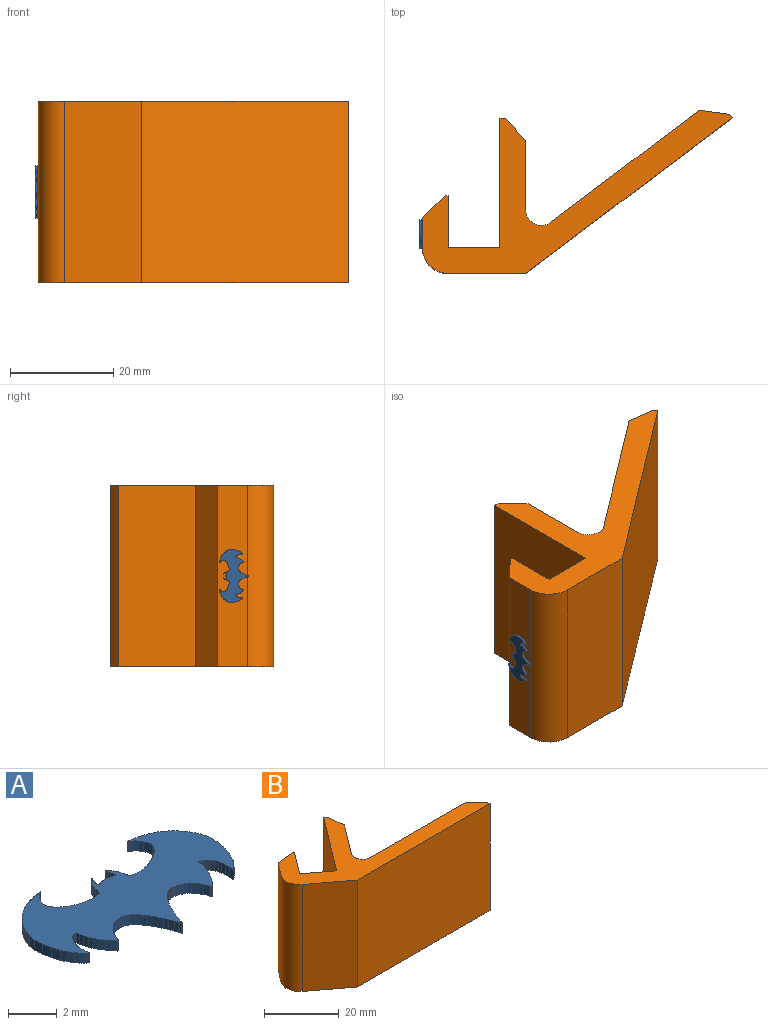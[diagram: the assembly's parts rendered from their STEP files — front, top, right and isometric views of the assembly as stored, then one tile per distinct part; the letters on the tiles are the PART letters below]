
ASSEMBLY  parts=2 mates=1
PART A: 225 faces, bbox 10.2x5.7x0.5 mm
  f0: cylinder r=2.47mm len=0.5mm, axis (0,0,1), area 0mm2, adj f1,f222,f223,f224
  f1: cylinder r=1.36mm len=0.5mm, axis (0,0,1), area 0.1mm2, adj f0,f2,f223,f224
  f2: cylinder r=7.6mm len=0.5mm, axis (0,0,1), area 0.1mm2, adj f1,f3,f223,f224
  f3: cylinder r=7.45mm len=0.5mm, axis (0,0,1), area 0.1mm2, adj f2,f4,f223,f224
  f4: cylinder r=1.87mm len=0.5mm, axis (0,0,1), area 0.1mm2, adj f3,f5,f223,f224
  f5: cylinder r=2.14mm len=0.5mm, axis (0,0,1), area 0.1mm2, adj f4,f6,f223,f224
  f6: cylinder r=2.99mm len=0.5mm, axis (0,0,1), area 0.1mm2, adj f5,f7,f223,f224
  f7: cylinder r=3.14mm len=0.5mm, axis (0,0,1), area 0.2mm2, adj f6,f8,f223,f224
  f8: cylinder r=2.81mm len=0.5mm, axis (0,0,1), area 0.1mm2, adj f7,f9,f223,f224
  f9: cylinder r=1.36mm len=0.5mm, axis (0,0,1), area 0.1mm2, adj f8,f10,f223,f224
  f10: cylinder r=4.82mm len=0.5mm, axis (0,0,1), area 0.1mm2, adj f9,f11,f223,f224
  f11: cylinder r=4.88mm len=0.5mm, axis (0,0,1), area 0.1mm2, adj f10,f12,f223,f224
  f12: cylinder r=1.99mm len=0.5mm, axis (0,0,1), area 0.1mm2, adj f11,f13,f223,f224
  f13: cylinder r=1.85mm len=0.5mm, axis (0,0,1), area 0.1mm2, adj f12,f14,f223,f224
  f14: cylinder r=3.8mm len=0.5mm, axis (0,0,1), area 0.1mm2, adj f13,f15,f223,f224
  f15: cylinder r=3.71mm len=0.5mm, axis (0,0,1), area 0.1mm2, adj f14,f16,f223,f224
  f16: cylinder r=1.26mm len=0.5mm, axis (0,0,1), area 0.1mm2, adj f15,f17,f223,f224
  f17: cylinder r=1.37mm len=0.5mm, axis (0,0,1), area 0.2mm2, adj f16,f18,f223,f224
  f18: cylinder r=3.17mm len=0.5mm, axis (0,0,1), area 0.2mm2, adj f17,f19,f223,f224
  f19: cylinder r=3.6mm len=0.5mm, axis (0,0,1), area 0.2mm2, adj f18,f20,f223,f224
  f20: cylinder r=3.26mm len=0.5mm, axis (0,0,1), area 0.2mm2, adj f19,f21,f223,f224
  f21: cylinder r=2.06mm len=0.5mm, axis (0,0,1), area 0.1mm2, adj f20,f22,f223,f224
  f22: cylinder r=3.13mm len=0.5mm, axis (0,0,1), area 0.1mm2, adj f21,f23,f223,f224
  f23: cylinder r=2.96mm len=0.5mm, axis (0,0,1), area 0.1mm2, adj f22,f24,f223,f224
  f24: cylinder r=1.3mm len=0.5mm, axis (0,0,1), area 0.1mm2, adj f23,f25,f223,f224
  f25: plane 0.5x0.09mm, normal (-0.63,-0.77,0), area 0.1mm2, adj f24,f26,f223,f224
  f26: plane 0.5x0.26mm, normal (1,0.05,0), area 0.1mm2, adj f25,f27,f223,f224
  f27: cylinder r=2.86mm len=0.5mm, axis (0,0,1), area 0.1mm2, adj f26,f28,f223,f224
  f28: cylinder r=1.47mm len=0.5mm, axis (0,0,1), area 0.1mm2, adj f27,f29,f223,f224
  f29: cylinder r=1.17mm len=0.5mm, axis (0,0,1), area 0.1mm2, adj f28,f30,f223,f224
  f30: cylinder r=1.1mm len=0.5mm, axis (0,0,1), area 0.1mm2, adj f29,f31,f223,f224
  f31: cylinder r=1.32mm len=0.5mm, axis (0,0,1), area 0.1mm2, adj f30,f32,f223,f224
  f32: cylinder r=0.63mm len=0.5mm, axis (0,0,1), area 0.1mm2, adj f31,f33,f223,f224
  f33: cylinder r=0.5mm len=0.5mm, axis (0,0,1), area 0.1mm2, adj f32,f34,f223,f224
  f34: cylinder r=0.57mm len=0.5mm, axis (0,0,1), area 0.1mm2, adj f33,f35,f223,f224
  f35: plane 0.5x0.07mm, normal (0.18,-0.98,0), area 0mm2, adj f34,f36,f223,f224
  f36: plane 0.5x0.19mm, normal (-0.99,-0.13,0), area 0.1mm2, adj f35,f37,f223,f224
  f37: cylinder r=1.78mm len=0.5mm, axis (0,0,1), area 0.1mm2, adj f36,f38,f223,f224
  f38: cylinder r=1.73mm len=0.5mm, axis (0,0,1), area 0.1mm2, adj f37,f39,f223,f224
  f39: cylinder r=2.05mm len=0.5mm, axis (0,0,1), area 0.1mm2, adj f38,f40,f223,f224
  f40: cylinder r=3.63mm len=0.5mm, axis (0,0,1), area 0.1mm2, adj f39,f41,f223,f224
  f41: cylinder r=3.24mm len=0.5mm, axis (0,0,1), area 0.1mm2, adj f40,f42,f223,f224
  f42: cylinder r=6.22mm len=0.5mm, axis (0,0,1), area 0.1mm2, adj f41,f43,f223,f224
  f43: cylinder r=16.14mm len=0.5mm, axis (0,0,1), area 0.1mm2, adj f42,f44,f223,f224
  f44: cylinder r=0.06mm len=0.5mm, axis (0,0,1), area 0mm2, adj f43,f45,f223,f224
  f45: cylinder r=0.01mm len=0.5mm, axis (0,0,1), area 0mm2, adj f44,f46,f223,f224
  f46: cylinder r=0.57mm len=0.5mm, axis (0,0,1), area 0mm2, adj f45,f47,f223,f224
  f47: cylinder r=0.56mm len=0.5mm, axis (0,0,1), area 0mm2, adj f46,f48,f223,f224
  f48: cylinder r=1.02mm len=0.5mm, axis (0,0,1), area 0mm2, adj f47,f49,f223,f224
  f49: cylinder r=1.42mm len=0.5mm, axis (0,0,1), area 0.1mm2, adj f48,f50,f223,f224
  f50: cylinder r=1.9mm len=0.5mm, axis (0,0,1), area 0.1mm2, adj f49,f51,f223,f224
  f51: cylinder r=1.82mm len=0.5mm, axis (0,0,1), area 0.1mm2, adj f50,f52,f223,f224
  f52: cylinder r=1.13mm len=0.5mm, axis (0,0,1), area 0.1mm2, adj f51,f53,f223,f224
  f53: cylinder r=1.01mm len=0.5mm, axis (0,0,1), area 0.1mm2, adj f52,f54,f223,f224
  f54: cylinder r=1.15mm len=0.5mm, axis (0,0,1), area 0.1mm2, adj f53,f55,f223,f224
  f55: cylinder r=1.04mm len=0.5mm, axis (0,0,1), area 0.1mm2, adj f54,f56,f223,f224
  f56: cylinder r=0.56mm len=0.5mm, axis (0,0,1), area 0.1mm2, adj f55,f57,f223,f224
  f57: cylinder r=0.72mm len=0.5mm, axis (0,0,1), area 0.1mm2, adj f56,f58,f223,f224
  f58: cylinder r=1.73mm len=0.5mm, axis (0,0,1), area 0.2mm2, adj f57,f59,f223,f224
  f59: cylinder r=2.47mm len=0.5mm, axis (0,0,1), area 0.2mm2, adj f58,f60,f223,f224
  f60: cylinder r=4.3mm len=0.5mm, axis (0,0,1), area 0.2mm2, adj f59,f61,f223,f224
  f61: cylinder r=5.97mm len=0.5mm, axis (0,0,1), area 0.1mm2, adj f60,f62,f223,f224
  f62: cylinder r=7.82mm len=0.5mm, axis (0,0,1), area 0.1mm2, adj f61,f63,f223,f224
  f63: cylinder r=7.49mm len=0.5mm, axis (0,0,1), area 0.1mm2, adj f62,f64,f223,f224
  f64: cylinder r=4.46mm len=0.5mm, axis (0,0,1), area 0.1mm2, adj f63,f65,f223,f224
  f65: cylinder r=2.06mm len=0.5mm, axis (0,0,1), area 0mm2, adj f64,f66,f223,f224
  f66: cylinder r=1.1mm len=0.5mm, axis (0,0,1), area 0mm2, adj f65,f67,f223,f224
  f67: cylinder r=1.96mm len=0.5mm, axis (0,0,1), area 0mm2, adj f66,f68,f223,f224
  f68: cylinder r=0.01mm len=0.5mm, axis (0,0,1), area 0mm2, adj f67,f69,f223,f224
  f69: cylinder r=1.96mm len=0.5mm, axis (0,0,1), area 0mm2, adj f68,f70,f223,f224
  f70: cylinder r=1.1mm len=0.5mm, axis (0,0,1), area 0mm2, adj f69,f71,f223,f224
  f71: cylinder r=2.06mm len=0.5mm, axis (0,0,1), area 0mm2, adj f70,f72,f223,f224
  f72: cylinder r=5.3mm len=0.5mm, axis (0,0,1), area 0.2mm2, adj f71,f73,f223,f224
  f73: cylinder r=6.68mm len=0.5mm, axis (0,0,1), area 0.2mm2, adj f72,f74,f223,f224
  f74: cylinder r=6.25mm len=0.5mm, axis (0,0,1), area 0.2mm2, adj f73,f75,f223,f224
  f75: cylinder r=3.36mm len=0.5mm, axis (0,0,1), area 0.2mm2, adj f74,f76,f223,f224
  f76: cylinder r=2.6mm len=0.5mm, axis (0,0,1), area 0.1mm2, adj f75,f77,f223,f224
  f77: cylinder r=1.69mm len=0.5mm, axis (0,0,1), area 0.1mm2, adj f76,f78,f223,f224
  f78: cylinder r=1.29mm len=0.5mm, axis (0,0,1), area 0.1mm2, adj f77,f79,f223,f224
  f79: cylinder r=0.66mm len=0.5mm, axis (0,0,1), area 0.1mm2, adj f78,f80,f223,f224
  f80: cylinder r=0.52mm len=0.5mm, axis (0,0,1), area 0.1mm2, adj f79,f81,f223,f224
  f81: cylinder r=1.14mm len=0.5mm, axis (0,0,1), area 0.1mm2, adj f80,f82,f223,f224
  f82: cylinder r=1.25mm len=0.5mm, axis (0,0,1), area 0.1mm2, adj f81,f83,f223,f224
  f83: cylinder r=0.97mm len=0.5mm, axis (0,0,1), area 0.1mm2, adj f82,f84,f223,f224
  f84: cylinder r=1.13mm len=0.5mm, axis (0,0,1), area 0.1mm2, adj f83,f85,f223,f224
  f85: cylinder r=1.82mm len=0.5mm, axis (0,0,1), area 0.1mm2, adj f84,f86,f223,f224
  f86: cylinder r=1.9mm len=0.5mm, axis (0,0,1), area 0.1mm2, adj f85,f87,f223,f224
  f87: cylinder r=1.42mm len=0.5mm, axis (0,0,1), area 0.1mm2, adj f86,f88,f223,f224
  f88: cylinder r=1.02mm len=0.5mm, axis (0,0,1), area 0mm2, adj f87,f89,f223,f224
  f89: cylinder r=0.56mm len=0.5mm, axis (0,0,1), area 0mm2, adj f88,f90,f223,f224
  f90: cylinder r=0.57mm len=0.5mm, axis (0,0,1), area 0mm2, adj f89,f91,f223,f224
  f91: cylinder r=0.01mm len=0.5mm, axis (0,0,1), area 0mm2, adj f90,f92,f223,f224
  f92: cylinder r=0.03mm len=0.5mm, axis (0,0,1), area 0mm2, adj f91,f93,f223,f224
  f93: cylinder r=6mm len=0.5mm, axis (0,0,1), area 0.1mm2, adj f92,f94,f223,f224
  f94: cylinder r=3.62mm len=0.5mm, axis (0,0,1), area 0.1mm2, adj f93,f95,f223,f224
  f95: cylinder r=6.4mm len=0.5mm, axis (0,0,1), area 0.1mm2, adj f94,f96,f223,f224
  f96: cylinder r=3.88mm len=0.5mm, axis (0,0,1), area 0.2mm2, adj f95,f97,f223,f224
  f97: cylinder r=2.69mm len=0.5mm, axis (0,0,1), area 0.2mm2, adj f96,f98,f223,f224
  f98: cylinder r=2.18mm len=0.5mm, axis (0,0,1), area 0.1mm2, adj f97,f99,f223,f224
  f99: cylinder r=1.38mm len=0.5mm, axis (0,0,1), area 0.1mm2, adj f98,f100,f223,f224
  f100: plane 0.5x0.15mm, normal (1,-0.09,0), area 0.1mm2, adj f99,f101,f223,f224
  f101: plane 0.5x0.07mm, normal (-0.18,-0.98,0), area 0mm2, adj f100,f102,f223,f224
  f102: cylinder r=0.57mm len=0.5mm, axis (0,0,1), area 0.1mm2, adj f101,f103,f223,f224
  f103: cylinder r=0.5mm len=0.5mm, axis (0,0,1), area 0.1mm2, adj f102,f104,f223,f224
  f104: cylinder r=0.62mm len=0.5mm, axis (0,0,1), area 0.1mm2, adj f103,f105,f223,f224
  f105: cylinder r=1.32mm len=0.5mm, axis (0,0,1), area 0.1mm2, adj f104,f106,f223,f224
  f106: cylinder r=1.1mm len=0.5mm, axis (0,0,1), area 0.1mm2, adj f105,f107,f223,f224
  f107: cylinder r=1.17mm len=0.5mm, axis (0,0,1), area 0.1mm2, adj f106,f108,f223,f224
  f108: cylinder r=1.47mm len=0.5mm, axis (0,0,1), area 0.1mm2, adj f107,f109,f223,f224
  f109: cylinder r=2.84mm len=0.5mm, axis (0,0,1), area 0.1mm2, adj f108,f110,f223,f224
  f110: plane 0.5x0.26mm, normal (-1,0.05,0), area 0.1mm2, adj f109,f111,f223,f224
  f111: plane 0.5x0.08mm, normal (0.62,-0.78,0), area 0.1mm2, adj f110,f112,f223,f224
  f112: cylinder r=0.87mm len=0.5mm, axis (0,0,1), area 0.1mm2, adj f111,f113,f223,f224
  f113: cylinder r=2.65mm len=0.5mm, axis (0,0,1), area 0.1mm2, adj f112,f114,f223,f224
  f114: cylinder r=3.1mm len=0.5mm, axis (0,0,1), area 0.1mm2, adj f113,f115,f223,f224
  f115: cylinder r=3.08mm len=0.5mm, axis (0,0,1), area 0.1mm2, adj f114,f116,f223,f224
  f116: cylinder r=2.19mm len=0.5mm, axis (0,0,1), area 0.2mm2, adj f115,f117,f223,f224
  f117: cylinder r=3.23mm len=0.5mm, axis (0,0,1), area 0.2mm2, adj f116,f118,f223,f224
  f118: cylinder r=3.43mm len=0.5mm, axis (0,0,1), area 0.2mm2, adj f117,f119,f223,f224
  f119: cylinder r=3.06mm len=0.5mm, axis (0,0,1), area 0.2mm2, adj f118,f120,f223,f224
  f120: cylinder r=2.13mm len=0.5mm, axis (0,0,1), area 0.1mm2, adj f119,f121,f223,f224
  f121: cylinder r=1.28mm len=0.5mm, axis (0,0,1), area 0.1mm2, adj f120,f122,f223,f224
  f122: cylinder r=1.35mm len=0.5mm, axis (0,0,1), area 0.1mm2, adj f121,f123,f223,f224
  f123: cylinder r=2.58mm len=0.5mm, axis (0,0,1), area 0.1mm2, adj f122,f124,f223,f224
  f124: cylinder r=4.55mm len=0.5mm, axis (0,0,1), area 0.1mm2, adj f123,f125,f223,f224
  f125: cylinder r=1.94mm len=0.5mm, axis (0,0,1), area 0.1mm2, adj f124,f126,f223,f224
  f126: cylinder r=2mm len=0.5mm, axis (0,0,1), area 0.1mm2, adj f125,f127,f223,f224
  f127: cylinder r=5.08mm len=0.5mm, axis (0,0,1), area 0.1mm2, adj f126,f128,f223,f224
  f128: cylinder r=2.72mm len=0.5mm, axis (0,0,1), area 0.2mm2, adj f127,f129,f223,f224
  f129: cylinder r=2.51mm len=0.5mm, axis (0,0,1), area 0.2mm2, adj f128,f130,f223,f224
  f130: cylinder r=2.57mm len=0.5mm, axis (0,0,1), area 0.2mm2, adj f129,f131,f223,f224
  f131: cylinder r=2.99mm len=0.5mm, axis (0,0,1), area 0.2mm2, adj f130,f132,f223,f224
  f132: cylinder r=3.6mm len=0.5mm, axis (0,0,1), area 0.1mm2, adj f131,f133,f223,f224
  f133: cylinder r=4.3mm len=0.5mm, axis (0,0,1), area 0.1mm2, adj f132,f134,f223,f224
  f134: cylinder r=12.42mm len=0.5mm, axis (0,0,1), area 0.1mm2, adj f133,f135,f223,f224
  f135: cylinder r=0.01mm len=0.5mm, axis (0,0,1), area 0mm2, adj f134,f136,f223,f224
  f136: cylinder r=0.01mm len=0.5mm, axis (0,0,1), area 0mm2, adj f135,f137,f223,f224
  f137: cylinder r=1.56mm len=0.5mm, axis (0,0,1), area 0mm2, adj f136,f138,f223,f224
  f138: cylinder r=0.91mm len=0.5mm, axis (0,0,1), area 0mm2, adj f137,f139,f223,f224
  f139: cylinder r=1.65mm len=0.5mm, axis (0,0,1), area 0mm2, adj f138,f140,f223,f224
  f140: cylinder r=0.8mm len=0.5mm, axis (0,0,1), area 0.1mm2, adj f139,f141,f223,f224
  f141: cylinder r=1mm len=0.5mm, axis (0,0,1), area 0.1mm2, adj f140,f142,f223,f224
  f142: cylinder r=0.89mm len=0.5mm, axis (0,0,1), area 0.1mm2, adj f141,f143,f223,f224
  f143: cylinder r=0.45mm len=0.5mm, axis (0,0,1), area 0.1mm2, adj f142,f144,f223,f224
  f144: cylinder r=0.44mm len=0.5mm, axis (0,0,1), area 0.1mm2, adj f143,f145,f223,f224
  f145: cylinder r=1.11mm len=0.5mm, axis (0,0,1), area 0.1mm2, adj f144,f146,f223,f224
  f146: cylinder r=1.34mm len=0.5mm, axis (0,0,1), area 0.1mm2, adj f145,f147,f223,f224
  f147: cylinder r=1.46mm len=0.5mm, axis (0,0,1), area 0.1mm2, adj f146,f148,f223,f224
  f148: cylinder r=1.73mm len=0.5mm, axis (0,0,1), area 0.1mm2, adj f147,f149,f223,f224
  f149: cylinder r=4.09mm len=0.5mm, axis (0,0,1), area 0.1mm2, adj f148,f150,f223,f224
  f150: cylinder r=4.03mm len=0.5mm, axis (0,0,1), area 0.1mm2, adj f149,f151,f223,f224
  f151: cylinder r=1.36mm len=0.5mm, axis (0,0,1), area 0.1mm2, adj f150,f152,f223,f224
  f152: cylinder r=2.03mm len=0.5mm, axis (0,0,1), area 0.2mm2, adj f151,f153,f223,f224
  f153: cylinder r=2.3mm len=0.5mm, axis (0,0,1), area 0.2mm2, adj f152,f154,f223,f224
  f154: cylinder r=2.08mm len=0.5mm, axis (0,0,1), area 0.1mm2, adj f153,f155,f223,f224
  f155: cylinder r=0.17mm len=0.5mm, axis (0,0,1), area 0.1mm2, adj f154,f156,f223,f224
  f156: cylinder r=0.11mm len=0.5mm, axis (0,0,1), area 0mm2, adj f155,f157,f223,f224
  f157: cylinder r=1.9mm len=0.5mm, axis (0,0,1), area 0mm2, adj f156,f158,f223,f224
  f158: cylinder r=1.96mm len=0.5mm, axis (0,0,1), area 0mm2, adj f157,f159,f223,f224
  f159: cylinder r=2.56mm len=0.5mm, axis (0,0,1), area 0mm2, adj f158,f160,f223,f224
  f160: cylinder r=1.85mm len=0.5mm, axis (0,0,1), area 0.1mm2, adj f159,f161,f223,f224
  f161: cylinder r=0.86mm len=0.5mm, axis (0,0,1), area 0.1mm2, adj f160,f162,f223,f224
  f162: cylinder r=0.76mm len=0.5mm, axis (0,0,1), area 0.1mm2, adj f161,f163,f223,f224
  f163: cylinder r=1.16mm len=0.5mm, axis (0,0,1), area 0.1mm2, adj f162,f164,f223,f224
  f164: cylinder r=2.82mm len=0.5mm, axis (0,0,1), area 0.1mm2, adj f163,f165,f223,f224
  f165: cylinder r=0.1mm len=0.5mm, axis (0,0,1), area 0mm2, adj f164,f166,f223,f224
  f166: cylinder r=0.01mm len=0.5mm, axis (0,0,1), area 0mm2, adj f165,f167,f223,f224
  f167: cylinder r=0.35mm len=0.5mm, axis (0,0,1), area 0mm2, adj f166,f168,f223,f224
  f168: cylinder r=0.44mm len=0.5mm, axis (0,0,1), area 0mm2, adj f167,f169,f223,f224
  f169: cylinder r=1.93mm len=0.5mm, axis (0,0,1), area 0.1mm2, adj f168,f170,f223,f224
  f170: cylinder r=1.92mm len=0.5mm, axis (0,0,1), area 0.1mm2, adj f169,f171,f223,f224
  f171: cylinder r=0.48mm len=0.5mm, axis (0,0,1), area 0mm2, adj f170,f172,f223,f224
  f172: cylinder r=0.25mm len=0.5mm, axis (0,0,1), area 0mm2, adj f171,f173,f223,f224
  f173: cylinder r=0.01mm len=0.5mm, axis (0,0,1), area 0mm2, adj f172,f174,f223,f224
  f174: cylinder r=0.09mm len=0.5mm, axis (0,0,1), area 0mm2, adj f173,f175,f223,f224
  f175: cylinder r=17.8mm len=0.5mm, axis (0,0,1), area 0.1mm2, adj f174,f176,f223,f224
  f176: cylinder r=0.68mm len=0.5mm, axis (0,0,1), area 0.1mm2, adj f175,f177,f223,f224
  f177: cylinder r=1.28mm len=0.5mm, axis (0,0,1), area 0.1mm2, adj f176,f178,f223,f224
  f178: cylinder r=1.28mm len=0.5mm, axis (0,0,1), area 0.1mm2, adj f177,f179,f223,f224
  f179: cylinder r=0.68mm len=0.5mm, axis (0,0,1), area 0.1mm2, adj f178,f180,f223,f224
  f180: cylinder r=17.8mm len=0.5mm, axis (0,0,1), area 0.1mm2, adj f179,f181,f223,f224
  f181: cylinder r=0.09mm len=0.5mm, axis (0,0,1), area 0mm2, adj f180,f182,f223,f224
  f182: cylinder r=0.01mm len=0.5mm, axis (0,0,1), area 0mm2, adj f181,f183,f223,f224
  f183: cylinder r=0.25mm len=0.5mm, axis (0,0,1), area 0mm2, adj f182,f184,f223,f224
  f184: cylinder r=0.48mm len=0.5mm, axis (0,0,1), area 0mm2, adj f183,f185,f223,f224
  f185: cylinder r=1.92mm len=0.5mm, axis (0,0,1), area 0.1mm2, adj f184,f186,f223,f224
  f186: cylinder r=1.93mm len=0.5mm, axis (0,0,1), area 0.1mm2, adj f185,f187,f223,f224
  f187: cylinder r=0.44mm len=0.5mm, axis (0,0,1), area 0mm2, adj f186,f188,f223,f224
  f188: cylinder r=0.35mm len=0.5mm, axis (0,0,1), area 0mm2, adj f187,f189,f223,f224
  f189: cylinder r=0.01mm len=0.5mm, axis (0,0,1), area 0mm2, adj f188,f190,f223,f224
  f190: cylinder r=0.1mm len=0.5mm, axis (0,0,1), area 0mm2, adj f189,f191,f223,f224
  f191: cylinder r=2.82mm len=0.5mm, axis (0,0,1), area 0.1mm2, adj f190,f192,f223,f224
  f192: cylinder r=1.18mm len=0.5mm, axis (0,0,1), area 0.1mm2, adj f191,f193,f223,f224
  f193: cylinder r=0.78mm len=0.5mm, axis (0,0,1), area 0.1mm2, adj f192,f194,f223,f224
  f194: cylinder r=0.81mm len=0.5mm, axis (0,0,1), area 0.1mm2, adj f193,f195,f223,f224
  f195: cylinder r=1.34mm len=0.5mm, axis (0,0,1), area 0.1mm2, adj f194,f196,f223,f224
  f196: cylinder r=3.11mm len=0.5mm, axis (0,0,1), area 0.1mm2, adj f195,f197,f223,f224
  f197: cylinder r=0.2mm len=0.5mm, axis (0,0,1), area 0.1mm2, adj f196,f198,f223,f224
  f198: cylinder r=0.16mm len=0.5mm, axis (0,0,1), area 0mm2, adj f197,f199,f223,f224
  f199: cylinder r=1.88mm len=0.5mm, axis (0,0,1), area 0.1mm2, adj f198,f200,f223,f224
  f200: cylinder r=1.12mm len=0.5mm, axis (0,0,1), area 0.1mm2, adj f199,f201,f223,f224
  f201: cylinder r=2.49mm len=0.5mm, axis (0,0,1), area 0.1mm2, adj f200,f202,f223,f224
  f202: cylinder r=2.64mm len=0.5mm, axis (0,0,1), area 0.1mm2, adj f201,f203,f223,f224
  f203: cylinder r=1.81mm len=0.5mm, axis (0,0,1), area 0.1mm2, adj f202,f204,f223,f224
  f204: cylinder r=1.38mm len=0.5mm, axis (0,0,1), area 0.1mm2, adj f203,f205,f223,f224
  f205: cylinder r=4.01mm len=0.5mm, axis (0,0,1), area 0.1mm2, adj f204,f206,f223,f224
  f206: cylinder r=4.06mm len=0.5mm, axis (0,0,1), area 0.1mm2, adj f205,f207,f223,f224
  f207: cylinder r=1.74mm len=0.5mm, axis (0,0,1), area 0.1mm2, adj f206,f208,f223,f224
  f208: cylinder r=1.46mm len=0.5mm, axis (0,0,1), area 0.1mm2, adj f207,f209,f223,f224
  f209: cylinder r=1.34mm len=0.5mm, axis (0,0,1), area 0.1mm2, adj f208,f210,f223,f224
  f210: cylinder r=1.11mm len=0.5mm, axis (0,0,1), area 0.1mm2, adj f209,f211,f223,f224
  f211: cylinder r=0.44mm len=0.5mm, axis (0,0,1), area 0.1mm2, adj f210,f212,f223,f224
  f212: cylinder r=0.45mm len=0.5mm, axis (0,0,1), area 0.1mm2, adj f211,f213,f223,f224
  f213: cylinder r=0.89mm len=0.5mm, axis (0,0,1), area 0.1mm2, adj f212,f214,f223,f224
  f214: cylinder r=1mm len=0.5mm, axis (0,0,1), area 0.1mm2, adj f213,f215,f223,f224
  f215: cylinder r=0.8mm len=0.5mm, axis (0,0,1), area 0.1mm2, adj f214,f216,f223,f224
  f216: cylinder r=2.13mm len=0.5mm, axis (0,0,1), area 0mm2, adj f215,f217,f223,f224
  f217: cylinder r=1.15mm len=0.5mm, axis (0,0,1), area 0mm2, adj f216,f218,f223,f224
  f218: cylinder r=2.5mm len=0.5mm, axis (0,0,1), area 0mm2, adj f217,f219,f223,f224
  f219: cylinder r=0.01mm len=0.5mm, axis (0,0,1), area 0mm2, adj f218,f220,f223,f224
  f220: cylinder r=0.01mm len=0.5mm, axis (0,0,1), area 0mm2, adj f219,f221,f223,f224
  f221: cylinder r=3.38mm len=0.5mm, axis (0,0,1), area 0mm2, adj f220,f222,f223,f224
  f222: cylinder r=1.59mm len=0.5mm, axis (0,0,1), area 0mm2, adj f0,f221,f223,f224
  f223: plane 10.24x5.69mm, normal (0,0,-1), area 28.9mm2, adj f0,f1,f2,f3,f4,f5,f6,f7
  f224: plane 10.24x5.69mm, normal (0,0,1), area 28.9mm2, adj f0,f1,f2,f3,f4,f5,f6,f7
PART B: 18 faces, bbox 64x27x35 mm
  f0: plane 35x7.98mm, normal (0.6,0.8,0), area 350mm2, adj f1,f11,f12,f13
  f1: plane 35x7.98mm, normal (0.8,-0.6,0), area 350mm2, adj f0,f2,f12,f13
  f2: plane 35x0.44mm, normal (0.64,0.77,0), area 20.1mm2, adj f1,f12,f13,f15
  f3: plane 35x4.65mm, normal (-0.8,0.6,0), area 203.9mm2, adj f12,f13,f14,f15
  f4: plane 35x11.97mm, normal (-0.6,-0.8,0), area 525mm2, adj f5,f12,f13,f14
  f5: plane 50x35mm, normal (0,-1,0), area 1750mm2, adj f4,f6,f12,f13
  f6: plane 35x0.79mm, normal (1,0,0), area 27.6mm2, adj f5,f12,f13,f16
  f7: plane 35.99x35mm, normal (0,1,0), area 1259.6mm2, adj f8,f12,f13,f16
  f8: cylinder r=3mm len=35mm, axis (0,0,-1), area 232.9mm2, adj f7,f9,f12,f13
  f9: plane 35x10.73mm, normal (0.8,-0.6,0), area 470.8mm2, adj f8,f12,f13,f17
  f10: plane 35x0.77mm, normal (0.64,0.77,0), area 35.2mm2, adj f11,f12,f13,f17
  f11: plane 35x19.95mm, normal (-0.8,0.6,0), area 875mm2, adj f0,f10,f12,f13
  f12: plane 63.96x26.95mm, normal (0,0,1), area 491.6mm2, adj f0,f1,f2,f3,f4,f5,f6,f7
  f13: plane 63.96x26.95mm, normal (0,0,-1), area 491.6mm2, adj f0,f1,f2,f3,f4,f5,f6,f7
  f14: cylinder r=5mm len=35mm, axis (0,0,1), area 274.9mm2, adj f3,f4,f12,f13
  f15: plane 35x6.07mm, normal (-0.11,0.99,0), area 213.7mm2, adj f2,f3,f12,f13
  f16: plane 35x4.21mm, normal (0.71,0.71,0), area 208.4mm2, adj f6,f7,f12,f13
  f17: plane 35x5.76mm, normal (0.99,0.11,0), area 203mm2, adj f9,f10,f12,f13
PLACE A rot(axis=(0,-1,0),90deg) t=(-40.25,14.21,9.4)mm
PLACE B rot(axis=(0,0,1),37.1deg) t=(-24.64,15.17,-8.1)mm
MATE planar B.f3 <-> A.f223  axis (-1,0,0) through (-39.75,14.5,9.4)mm
